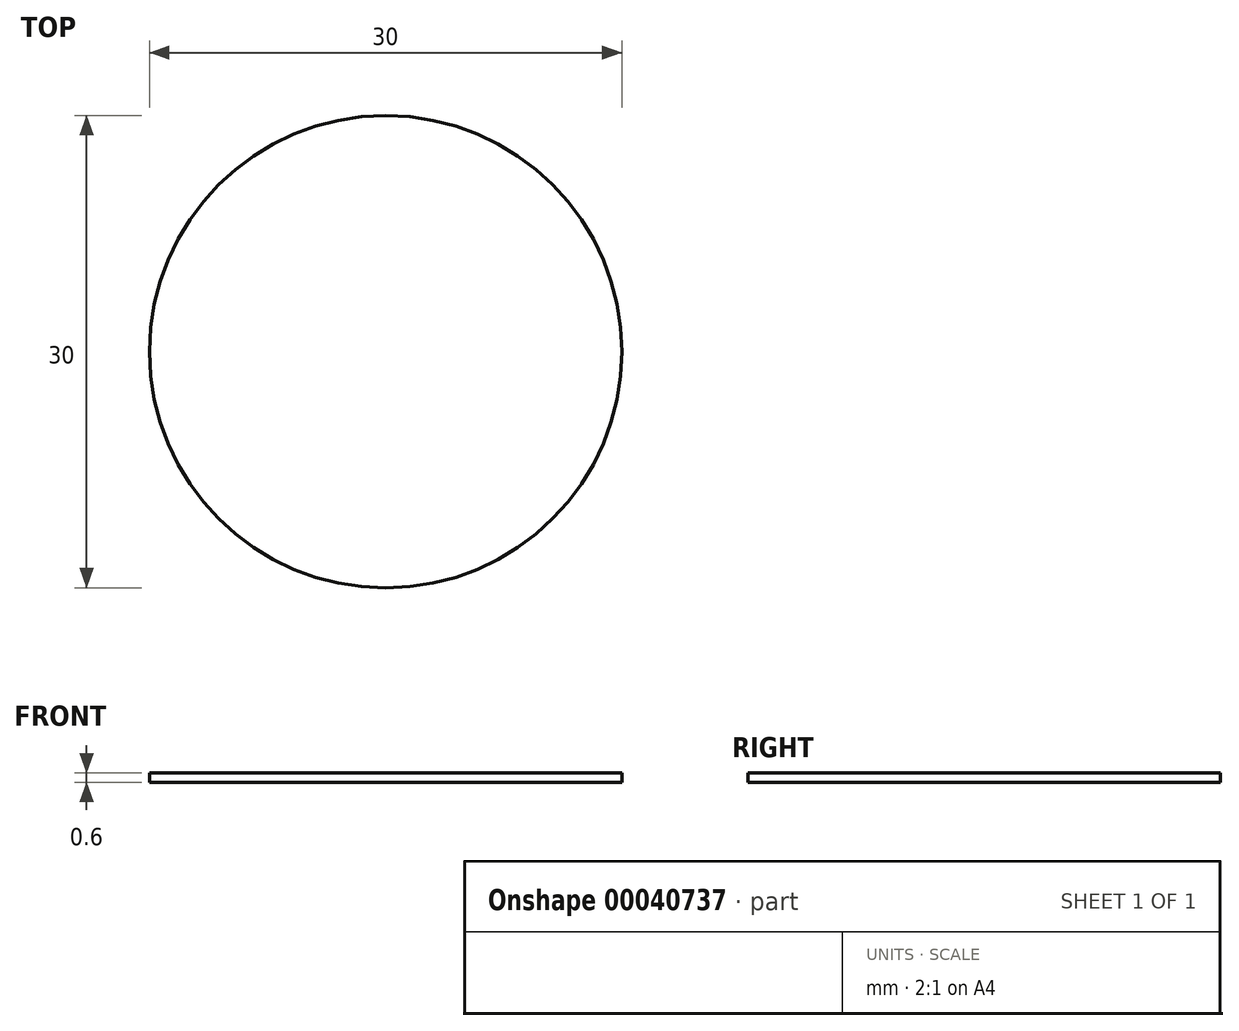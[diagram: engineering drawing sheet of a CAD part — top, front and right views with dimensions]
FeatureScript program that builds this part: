
annotation { "Feature Type Name" : "Feature", "Feature Type Description" : "" }
export const myFeature = defineFeature(function(context is Context, id is Id, definition is map)
    precondition{}
    {
        {
            var Q0;
            Q0=qCreatedBy(makeId("Top.planeOp"),FACE);
            var sketch = newSketch(context, id + "F0", { "sketchPlane" : qUnion([Q0])});
            skCircle(sketch, "E0", {"center": v(0.67, 0) * mm, "radius": 15 * mm});
            skSolve(sketch);
        }
        {
            var Q0;
            Q0=makeQuery(id+"F0.imprint","IMPRINT",FACE,{"disambiguationData":[TD([[makeQuery(id+"F0.imprint","IMPRINT",EDGE,{"derivedFrom":sQuery(id+"F0.wireOp",EDGE,"E0")}),1.0]])]});
            extrude(context, id + "F1", {"entities" : qUnion([Q0]), "depth" : .6 * mm});
        }
    });
